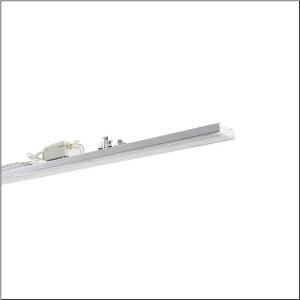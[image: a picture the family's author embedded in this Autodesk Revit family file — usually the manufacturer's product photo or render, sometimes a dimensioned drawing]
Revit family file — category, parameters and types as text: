
# Revit family: licross_r__21_recessed_ho_52te18mn4e5m_3244
name_source: partatom
category: Lighting Fixtures
units: mm (PartAtom-declared; Revit-internal decimal feet)

## family parameters
Cut with Voids When Loaded = No
Host = Face
Light Source = No
Part Type = Normal
Room Calculation Point = No
Round Connector Dimension = Use Diameter
Shared = No

## types (1)
- --- (1 x LED, 14940 lm, 83.1 W, 4000K)
    Apparent Load = 83 VA
    CIE Flux Codes = 75 94 99 100 100
    Color Rendering = 80
    Color Temperature = 4000K
    Default Elevation = 1800 mm
    Description = Licross® 21 Recessed HO, luminaire insert, of sheet steel, galvanised, coil coated, white, length: 1.500mm, width: 66mm, height: 67mm, LED rated luminous flux: 14.940lm, light colour: 840, control gear: ON/OFF Multilumen, with plug, 3-pole, with phase selection, mains connection: 220..240V, AC, 50/60Hz, rated input power: 83W, halogen-free wiring, primary light control with lens, of plastic, primary optical cover: cover, of PMMA, light emission: direct distribution, primary light characteristic: symmetric, protection rating (complete): IP54, insulation class (complete): insulation class I (protective earthing), certification: CE, ENEC, VDE, UKCA, protection symbol: D if used in an environment with non-conductive dust loads with corresponding accessories, impact resistance: IK06, permissible ambient temperature for indoor applications: -35..+30°C, corresponds to IFS (International Featured Standards) requirements for safety and quality in the food industry, reducing of maximum allowable ambient temperature of 5°C with ceiling mounting, LABS conformity tested according to VDMA 24364:2018-05, packaging unit: 1 piece
    Height = 58 mm
    Lamp = 1 x LED
    Lamp Light Flux = 14940 lm
    Lamp Power = 83.1 W
    Lamp count = 1
    Length = 1500 mm
    Luminous efficacy = 180 lm/W
    Manufacturer = Siteco
    ModVariant = No
    Model = 52TE18MN4E5M
    Mounting Place = Ceiling
    Mounting Type = Pendant
    Number of Poles = 1
    OnlyDefault = Yes
    Power Factor = 1
    Product Name = Licross® 21 Recessed HO
    Product group = luminaire insert
    ProductGroupID = 901
    Protection Class = Protection class I
    Protection Degree = IP 54
    RLX_Detail_Level = 1
    RLX_Emergency_Light_Flux = 0 lm
    RLX_Emergency_Type = 0
    RLX_Emergency_Type_DB = No
    RlxData = <blob elided: 22273 chars, md5=fe2c643c>
    Socket = socket
    Standby Power = 0 W
    System Light Flux = 14940 lm
    System Power = 83 W
    Type Comments = factory setting: luminous flux: 100 % | (A | C | E) | 195 mA
    Type Image = l_1296930.jpg
    URL = http://relux.com
    VarID = @adj_038097
    Voltage = 0 V
    Weight = 0.00 kg
    Width = 66 mm

## geometry (parser evidence)
native form markers: Blend x4, Sweep x12
no freeform markers — native parametric forms only
